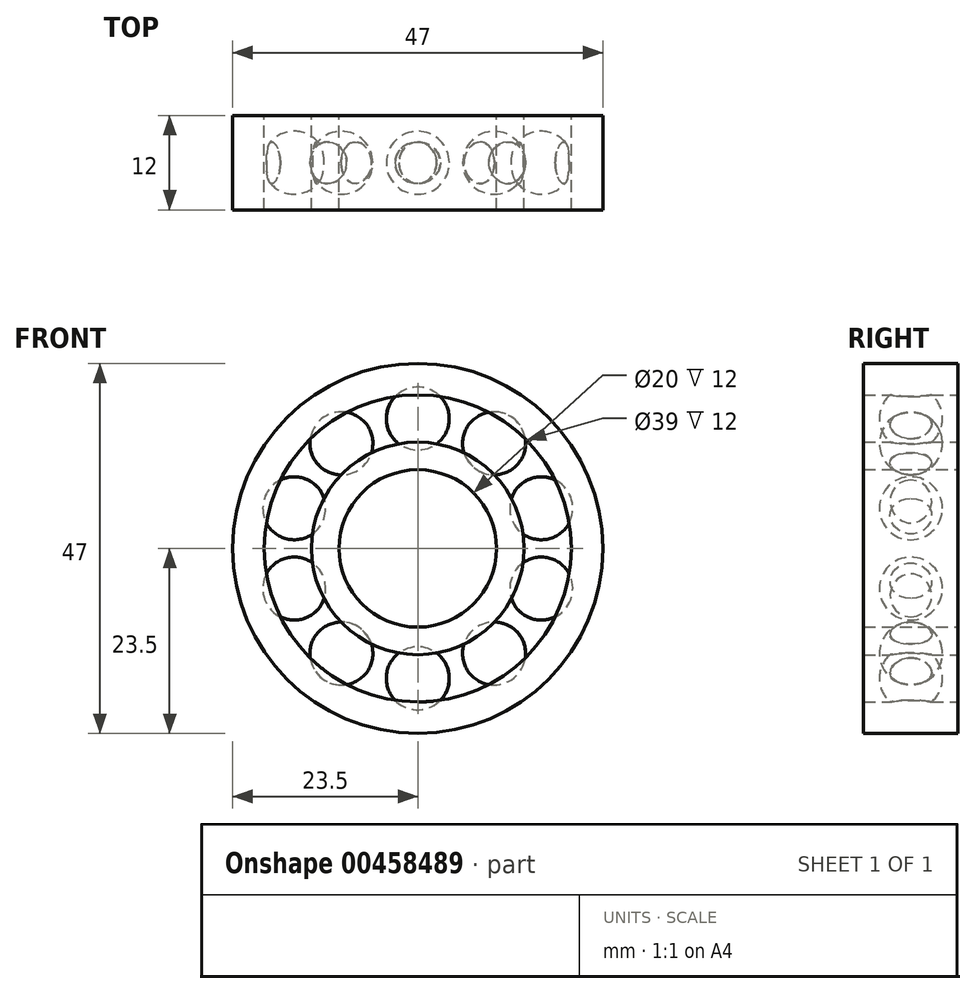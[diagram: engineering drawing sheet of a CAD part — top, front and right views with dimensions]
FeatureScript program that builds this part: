
annotation { "Feature Type Name" : "Feature", "Feature Type Description" : "" }
export const myFeature = defineFeature(function(context is Context, id is Id, definition is map)
    precondition{}
    {
        {
            var Q0;
            Q0=qCreatedBy(makeId("Front.planeOp"),FACE);
            var sketch = newSketch(context, id + "F0", { "sketchPlane" : qUnion([Q0])});
            skCircle(sketch, "E0", {"center": v(0, 0) * mm, "radius": 10 * mm});
            skCircle(sketch, "E1", {"center": v(0, 0) * mm, "radius": 13.5 * mm});
            skSolve(sketch);
        }
        {
            var Q0;
            Q0 = qSketchRegion(id + "F0", true);
            var Q1;
            Q1=makeQuery(id+"F0.imprint","IMPRINT",FACE,{"disambiguationData":[TD([[makeQuery(id+"F0.imprint","IMPRINT",EDGE,{"derivedFrom":sQuery(id+"F0.wireOp",EDGE,"E0")}),-1.0]])]});
            extrude(context, id + "F1", {"entities" : qUnion([Q0, Q1]), "depth" : 12 * mm, "symmetric" : true});
        }
        {
            var Q0;
            Q0=qCreatedBy(makeId("Front.planeOp"),FACE);
            var sketch = newSketch(context, id + "F2", { "sketchPlane" : qUnion([Q0])});
            skCircle(sketch, "E2", {"center": v(0, 0) * mm, "radius": 19.5 * mm});
            skCircle(sketch, "E3", {"center": v(0, 0) * mm, "radius": 23.5 * mm});
            skSolve(sketch);
        }
        {
            var Q0;
            Q0 = qSketchRegion(id + "F2", true);
            var Q1;
            Q1=makeQuery(id+"F2.imprint","IMPRINT",FACE,{"disambiguationData":[TD([[makeQuery(id+"F2.imprint","IMPRINT",EDGE,{"derivedFrom":sQuery(id+"F2.wireOp",EDGE,"E2")}),-1.0]])]});
            extrude(context, id + "F3", {"entities" : qUnion([Q0, Q1]), "depth" : 12 * mm, "symmetric" : true});
        }
        {
            var Q0;
            Q0=qCreatedBy(makeId("Front.planeOp"),FACE);
            var sketch = newSketch(context, id + "F4", { "sketchPlane" : qUnion([Q0])});
            skArc(sketch, "E4", {"start": v(0, 12.5) * mm, "mid": v(4, 16.5) * mm, "end": v(0, 20.5) * mm});
            skLineSegment(sketch, "E5", {"start": v(0, 20.5) * mm, "end": v(0, 12.5) * mm});
            skPoint(sketch, "E6.orphan", {"position": v(0, 21.45) * mm});
            skSolve(sketch);
        }
        {
            var Q0;
            Q0=makeQuery(id+"F4.imprint","IMPRINT",FACE,{"disambiguationData":[TD([[makeQuery(id+"F4.imprint","IMPRINT",EDGE,{"derivedFrom":sQuery(id+"F4.wireOp",EDGE,"E4")}),1.0]])]});
            var Q1;
            Q1=sQuery(id+"F4.wireOp",EDGE,"E5");
            revolve(context, id + "F5", {"entities" : qUnion([Q0]), "axis" : qUnion([Q1]), "revolveType" : RevolveType.FULL});
        }
        {
            var Q0;
            Q0=qCreatedBy(makeId("Top.planeOp"),FACE);
            var sketch = newSketch(context, id + "F6", { "sketchPlane" : qUnion([Q0])});
            skLineSegment(sketch, "E7", {"start": v(0, 0) * mm, "end": v(0, 11.76) * mm, "construction": true});
            skSolve(sketch);
        }
        {
            var Q0;
            Q0=makeQuery(id+"F5.opRevolve","SWEPT_BODY",BODY,{"disambiguationData":[OSD([sQuery(id+"F4.wireOp",EDGE,"E4"),sQuery(id+"F4.wireOp",EDGE,"E5")])]});
            var Q1;
            Q1=sQuery(id+"F6.wireOp",EDGE,"E7");
            circularPattern(context, id + "F7", {"operationType" : NewBodyOperationType.ADD, "entities" : qUnion([Q0]), "axis" : qUnion([Q1]), "angle" : 360 * degree, "instanceCount" : 10, "equalSpace" : true});
        }
    });
